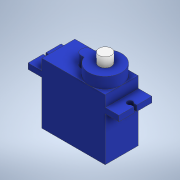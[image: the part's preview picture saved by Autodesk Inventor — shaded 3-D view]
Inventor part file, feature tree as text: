
AUTODESK INVENTOR PART (.ipt)
format: ipt  version: 2021 (Build 250183000, 183)  size: 185,856 bytes
history: native  units: mm
features: extrude x5, sketch x4
ambient origin geometry x8: Origin, YZ Plane, XZ Plane, XY Plane, X Axis, Y Axis, Z Axis, Center Point
bodies: Volumenkörper1 (feature_tree)
feature tree (9):
  sketch  "Skizze1"  dims[d0=23.0mm d1=22.0mm]
  extrude  "Extrusion1"  Depth=22.0mm
  extrude  "Extrusion2"  Depth=2.0mm
  extrude  "Extrusion3"  Depth=12.0mm TaperAngle=0.0deg
  extrude  "Extrusion4"  Depth=6.0mm
  extrude  "Extrusion5"  Depth=6.0mm
  sketch  "Skizze2"  dims[d2=16.0mm d3=2.0mm]
  sketch  "Skizze3"  dims[d4=5.0mm d5=12.0mm d6=0.0mm]
  sketch  "Skizze4"  dims[d7=12.0mm d8=0.0mm d9=6.0mm d10=6.0mm d11=4.0mm d12=4.0mm d13=0.0mm d14=2.0mm d15=2.0mm d16=2.0mm d17=2.0mm d18=1.0mm d19=2.0mm d20=0.0mm d21=4.5mm d22=6.0mm d23=3.5mm d24=0.0mm]
